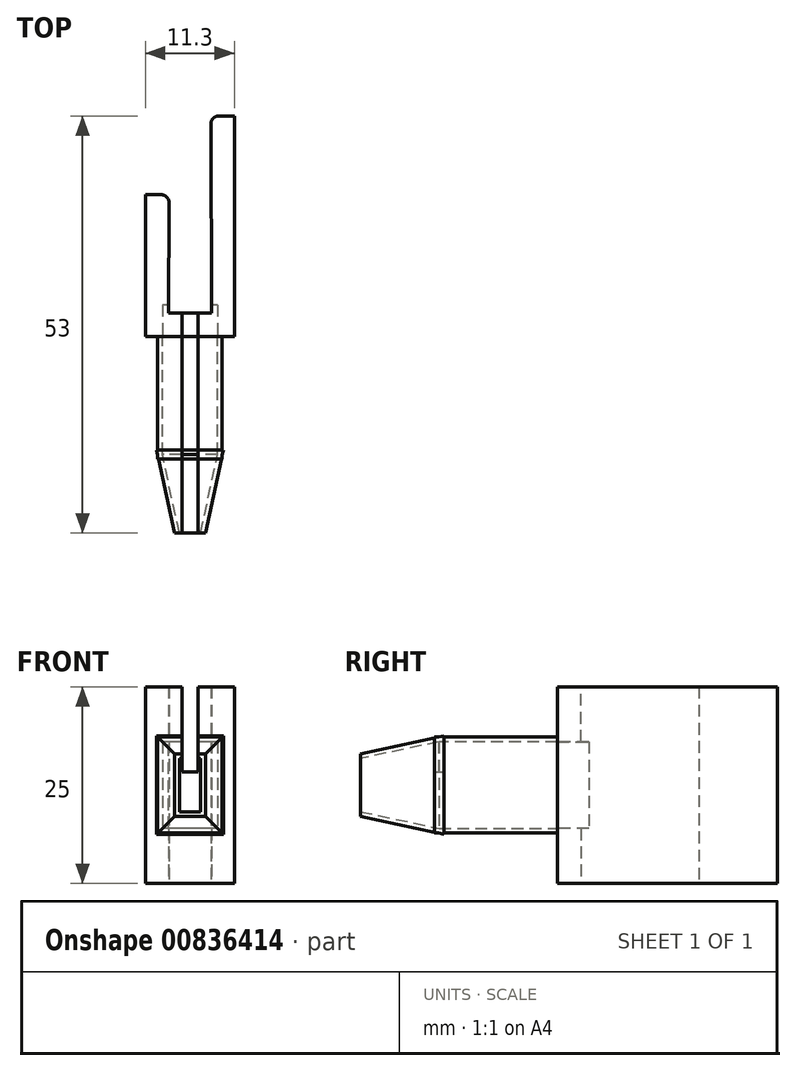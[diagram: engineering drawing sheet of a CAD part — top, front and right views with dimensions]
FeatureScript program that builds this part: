
annotation { "Feature Type Name" : "Feature", "Feature Type Description" : "" }
export const myFeature = defineFeature(function(context is Context, id is Id, definition is map)
    precondition{}
    {
        {
            var Q0;
            Q0=qCreatedBy(makeId("Top.planeOp"),FACE);
            var sketch = newSketch(context, id + "F0", { "sketchPlane" : qUnion([Q0])});
            skLineSegment(sketch, "E0", {"start": v(0, 0) * mm, "end": v(0, 28) * mm});
            skLineSegment(sketch, "E1", {"start": v(0, 28) * mm, "end": v(-3, 28) * mm});
            skLineSegment(sketch, "E2", {"start": v(-3, 28) * mm, "end": v(-2.9, 3) * mm});
            skLineSegment(sketch, "E3", {"start": v(-2.9, 3) * mm, "end": v(-8.4, 3) * mm});
            skLineSegment(sketch, "E4", {"start": v(-8.4, 3) * mm, "end": v(-8.3, 18) * mm});
            skLineSegment(sketch, "E5", {"start": v(-8.3, 18) * mm, "end": v(-11.3, 18) * mm});
            skLineSegment(sketch, "E6", {"start": v(-11.3, 18) * mm, "end": v(-11.3, 0) * mm});
            skLineSegment(sketch, "E7", {"start": v(-11.3, 0) * mm, "end": v(0, 0) * mm});
            skLineSegment(sketch, "E8", {"start": v(-8.4, 3) * mm, "end": v(-11.3, 3) * mm, "construction": true});
            skLineSegment(sketch, "E9", {"start": v(-2.9, 3) * mm, "end": v(0, 3) * mm, "construction": true});
            skSolve(sketch);
        }
        {
            var Q0;
            Q0=makeQuery(id+"F0.imprint","IMPRINT",FACE,{"disambiguationData":[TD([[makeQuery(id+"F0.imprint","IMPRINT",EDGE,{"derivedFrom":sQuery(id+"F0.wireOp",EDGE,"E0")}),1.0]])]});
            extrude(context, id + "F1", {"entities" : qUnion([Q0]), "depth" : 25 * mm, "offsetDistance" : 25 * mm});
        }
        {
            var Q0;
            Q0=makeQuery(id+"F1.opExtrude","SWEPT_FACE",FACE,{"disambiguationData":[OSD([sQuery(id+"F0.wireOp",EDGE,"E7")])]});
            var sketch = newSketch(context, id + "F2", { "sketchPlane" : qUnion([Q0])});
            skPoint(sketch, "E10.0", {"position": v(-8.4, 0) * mm});
            skPoint(sketch, "E11.0", {"position": v(-2.9, 0) * mm});
            skLineSegment(sketch, "E12", {"start": v(-2.9, 0) * mm, "end": v(-2.9, 25) * mm, "construction": true});
            skLineSegment(sketch, "E13", {"start": v(-8.4, 0) * mm, "end": v(-8.4, 25) * mm, "construction": true});
            skLineSegment(sketch, "E14", {"start": v(-8.4, 25) * mm, "end": v(-2.9, 0) * mm, "construction": true});
            skPoint(sketch, "E15", {"position": v(-5.65, 12.5) * mm});
            skLineSegment(sketch, "E16.bottom", {"start": v(-2.15, 18) * mm, "end": v(-9.15, 18) * mm});
            skLineSegment(sketch, "E16.top", {"start": v(-2.15, 7) * mm, "end": v(-9.15, 7) * mm});
            skLineSegment(sketch, "E16.left", {"start": v(-2.15, 18) * mm, "end": v(-2.15, 7) * mm});
            skLineSegment(sketch, "E16.right", {"start": v(-9.15, 18) * mm, "end": v(-9.15, 7) * mm});
            skSolve(sketch);
        }
        {
            var Q0;
            Q0=makeQuery(id+"F2.imprint","IMPRINT",FACE,{"disambiguationData":[TD([[makeQuery(id+"F2.imprint","IMPRINT",EDGE,{"derivedFrom":sQuery(id+"F2.wireOp",EDGE,"E16.bottom")}),1.0]])]});
            extrude(context, id + "F3", {"entities" : qUnion([Q0]), "operationType" : NewBodyOperationType.REMOVE, "oppositeDirection" : true, "depth" : 4 * mm, "offsetDistance" : 25 * mm});
        }
        {
            var Q0;
            Q0=makeQuery(id+"F2.imprint","IMPRINT",FACE,{"disambiguationData":[TD([[makeQuery(id+"F2.imprint","IMPRINT",EDGE,{"derivedFrom":sQuery(id+"F2.wireOp",EDGE,"E16.bottom")}),1.0]])]});
            extrude(context, id + "F4", {"entities" : qUnion([Q0]), "depth" : 15 * mm, "offsetDistance" : 25 * mm});
        }
        {
            var Q0;
            Q0=makeQuery(id+"F4.opExtrude","CAP_FACE",FACE,{"disambiguationData":[OSD([sQuery(id+"F2.wireOp",EDGE,"E16.bottom"),sQuery(id+"F2.wireOp",EDGE,"E16.top"),sQuery(id+"F2.wireOp",EDGE,"E16.left"),sQuery(id+"F2.wireOp",EDGE,"E16.right")])],"isStart":false});
            cPlane(context, id + "F5", {"entities" : qUnion([Q0]), "cplaneType" : CPlaneType.OFFSET, "offset" : 10 * mm, "width" : 150 * mm, "height" : 150 * mm});
        }
        {
            var Q0;
            Q0=qCreatedBy(id+"F5.planeOp",FACE);
            var sketch = newSketch(context, id + "F6", { "sketchPlane" : qUnion([Q0])});
            skPoint(sketch, "E17.0", {"position": v(-5.65, 12.5) * mm});
            skLineSegment(sketch, "E18.bottom", {"start": v(-4.3, 9.13) * mm, "end": v(-7, 9.13) * mm});
            skLineSegment(sketch, "E18.top", {"start": v(-4.3, 15.87) * mm, "end": v(-7, 15.87) * mm});
            skLineSegment(sketch, "E18.left", {"start": v(-4.3, 9.13) * mm, "end": v(-4.3, 15.87) * mm});
            skLineSegment(sketch, "E18.right", {"start": v(-7, 9.13) * mm, "end": v(-7, 15.87) * mm});
            skSolve(sketch);
        }
        {
            var Q0;
            Q0=makeQuery(id+"F6.imprint","IMPRINT",FACE,{"disambiguationData":[TD([[makeQuery(id+"F6.imprint","IMPRINT",EDGE,{"derivedFrom":sQuery(id+"F6.wireOp",EDGE,"E18.bottom")}),-1.0]])]});
            var Q1;
            Q1=makeQuery(id+"F4.opExtrude","CAP_FACE",FACE,{"disambiguationData":[OSD([sQuery(id+"F2.wireOp",EDGE,"E16.bottom"),sQuery(id+"F2.wireOp",EDGE,"E16.top"),sQuery(id+"F2.wireOp",EDGE,"E16.left"),sQuery(id+"F2.wireOp",EDGE,"E16.right")])],"isStart":false});
            loft(context, id + "F7", {"sheetProfilesArray" : [{ "sheetProfileEntities" : qUnion([Q0]) }, { "sheetProfileEntities" : qUnion([Q1]) }]});
        }
        {
            var Q0;
            Q0=makeQuery(id+"F4.opExtrude","CAP_FACE",FACE,{"disambiguationData":[OSD([sQuery(id+"F2.wireOp",EDGE,"E16.bottom"),sQuery(id+"F2.wireOp",EDGE,"E16.top"),sQuery(id+"F2.wireOp",EDGE,"E16.left"),sQuery(id+"F2.wireOp",EDGE,"E16.right")])],"isStart":true});
            var Q1;
            Q1=makeQuery(id+"F7.opLoft","CAP_FACE",FACE,{"disambiguationData":[OSD([makeQuery(id+"F6.imprint","IMPRINT",FACE,{"disambiguationData":[TD([[makeQuery(id+"F6.imprint","IMPRINT",EDGE,{"derivedFrom":sQuery(id+"F6.wireOp",EDGE,"E18.bottom")}),-1.0]])]})])],"isStart":true});
            shell(context, id + "F8", {"entities" : qUnion([Q0, Q1]), "thickness" : 0.6 * mm, "oppositeDirection" : true});
        }
        {
            var Q0;
            Q0=makeQuery(id+"F1.opExtrude","CAP_FACE",FACE,{"disambiguationData":[OSD([sQuery(id+"F0.wireOp",EDGE,"E0"),sQuery(id+"F0.wireOp",EDGE,"E1"),sQuery(id+"F0.wireOp",EDGE,"E2"),sQuery(id+"F0.wireOp",EDGE,"E3"),sQuery(id+"F0.wireOp",EDGE,"E4"),sQuery(id+"F0.wireOp",EDGE,"E5"),sQuery(id+"F0.wireOp",EDGE,"E6"),sQuery(id+"F0.wireOp",EDGE,"E7")])],"isStart":false});
            var sketch = newSketch(context, id + "F9", { "sketchPlane" : qUnion([Q0])});
            skLineSegment(sketch, "E19.bottom", {"start": v(-4.65, -40.9) * mm, "end": v(-6.65, -40.9) * mm});
            skLineSegment(sketch, "E19.top", {"start": v(-4.65, 40.9) * mm, "end": v(-6.65, 40.9) * mm});
            skLineSegment(sketch, "E19.left", {"start": v(-4.65, -40.9) * mm, "end": v(-4.65, 40.9) * mm});
            skLineSegment(sketch, "E19.right", {"start": v(-6.65, -40.9) * mm, "end": v(-6.65, 40.9) * mm});
            skPoint(sketch, "E19.middle", {"position": v(-5.65, 0) * mm});
            skSolve(sketch);
        }
        {
            var Q0;
            Q0 = qSketchRegion(id + "F9", true);
            extrude(context, id + "F10", {"entities" : qUnion([Q0]), "operationType" : NewBodyOperationType.REMOVE, "oppositeDirection" : true, "depth" : 10.8 * mm, "offsetDistance" : 25 * mm});
        }
        {
            var Q0;
            Q0=makeQuery(id+"F1.opExtrude","SWEPT_EDGE",EDGE,{"disambiguationData":[OSD([sQuery(id+"F0.wireOp",EDGE,"E1"),sQuery(id+"F0.wireOp",EDGE,"E2")])]});
            var Q1;
            Q1=makeQuery(id+"F1.opExtrude","SWEPT_EDGE",EDGE,{"disambiguationData":[OSD([sQuery(id+"F0.wireOp",EDGE,"E4"),sQuery(id+"F0.wireOp",EDGE,"E5")])]});
            fillet(context, id + "F11", {"entities" : qUnion([Q0, Q1]), "radius" : 1 * mm, "tangentPropagation" : true, "allowEdgeOverflow" : false});
        }
    });
